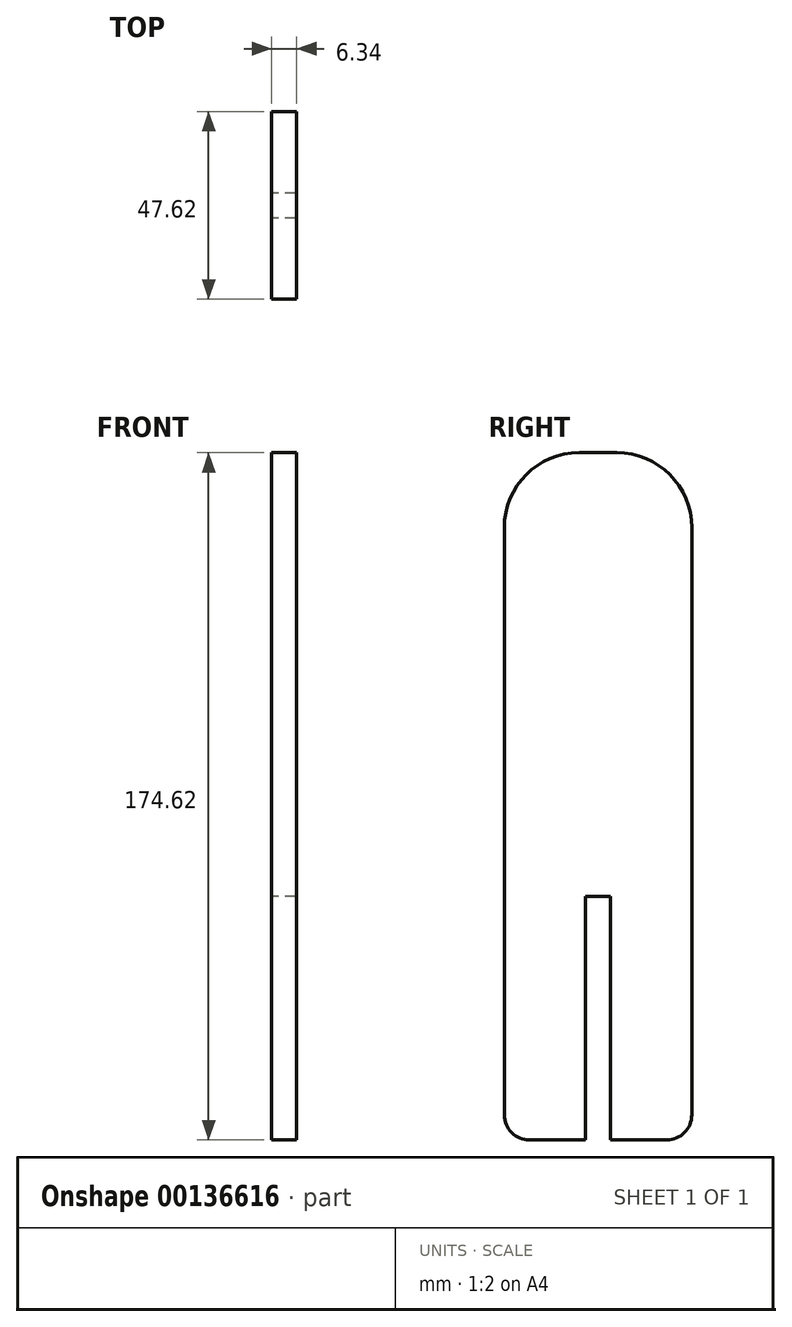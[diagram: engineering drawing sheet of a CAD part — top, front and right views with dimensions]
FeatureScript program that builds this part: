
annotation { "Feature Type Name" : "Feature", "Feature Type Description" : "" }
export const myFeature = defineFeature(function(context is Context, id is Id, definition is map)
    precondition{}
    {
        {
            var Q0;
            Q0=qCreatedBy(makeId("Right.planeOp"),FACE);
            var sketch = newSketch(context, id + "F0", { "sketchPlane" : qUnion([Q0])});
            skLineSegment(sketch, "E0.bottom", {"start": v(-4.76, 87.31) * mm, "end": v(4.76, 87.31) * mm});
            skLineSegment(sketch, "E0.top", {"start": v(-17.46, -87.31) * mm, "end": v(-3.17, -87.31) * mm});
            skLineSegment(sketch, "E0.left", {"start": v(-23.81, 68.26) * mm, "end": v(-23.81, -80.96) * mm});
            skLineSegment(sketch, "E0.right", {"start": v(23.81, 68.26) * mm, "end": v(23.81, -80.96) * mm});
            skPoint(sketch, "E1.visualSharp", {"position": v(-23.81, 87.31) * mm});
            skArc(sketch, "E1.filletArc", {"start": v(-4.76, 87.31) * mm, "mid": v(-18.23, 81.73) * mm, "end": v(-23.81, 68.26) * mm});
            skPoint(sketch, "E2.visualSharp", {"position": v(23.81, 87.31) * mm});
            skArc(sketch, "E2.filletArc", {"start": v(23.81, 68.26) * mm, "mid": v(18.23, 81.73) * mm, "end": v(4.76, 87.31) * mm});
            skLineSegment(sketch, "E3", {"start": v(3.18, -87.31) * mm, "end": v(3.18, -25.4) * mm});
            skLineSegment(sketch, "E4", {"start": v(3.18, -25.4) * mm, "end": v(-3.17, -25.4) * mm});
            skLineSegment(sketch, "E5", {"start": v(-3.17, -25.4) * mm, "end": v(-3.17, -87.31) * mm});
            skLineSegment(sketch, "E6.trimOffspring", {"start": v(3.18, -87.31) * mm, "end": v(17.46, -87.31) * mm});
            skPoint(sketch, "E7.visualSharp", {"position": v(-23.81, -87.31) * mm});
            skArc(sketch, "E7.filletArc", {"start": v(-23.81, -80.96) * mm, "mid": v(-21.95, -85.45) * mm, "end": v(-17.46, -87.31) * mm});
            skPoint(sketch, "E8.visualSharp", {"position": v(23.81, -87.31) * mm});
            skArc(sketch, "E8.filletArc", {"start": v(17.46, -87.31) * mm, "mid": v(21.95, -85.45) * mm, "end": v(23.81, -80.96) * mm});
            skSolve(sketch);
        }
        {
            var Q0;
            Q0 = qSketchRegion(id + "F0", true);
            extrude(context, id + "F1", {"entities" : qUnion([Q0]), "endBound" : BoundingType.SYMMETRIC, "depth" : 6.35 * mm});
        }
    });
